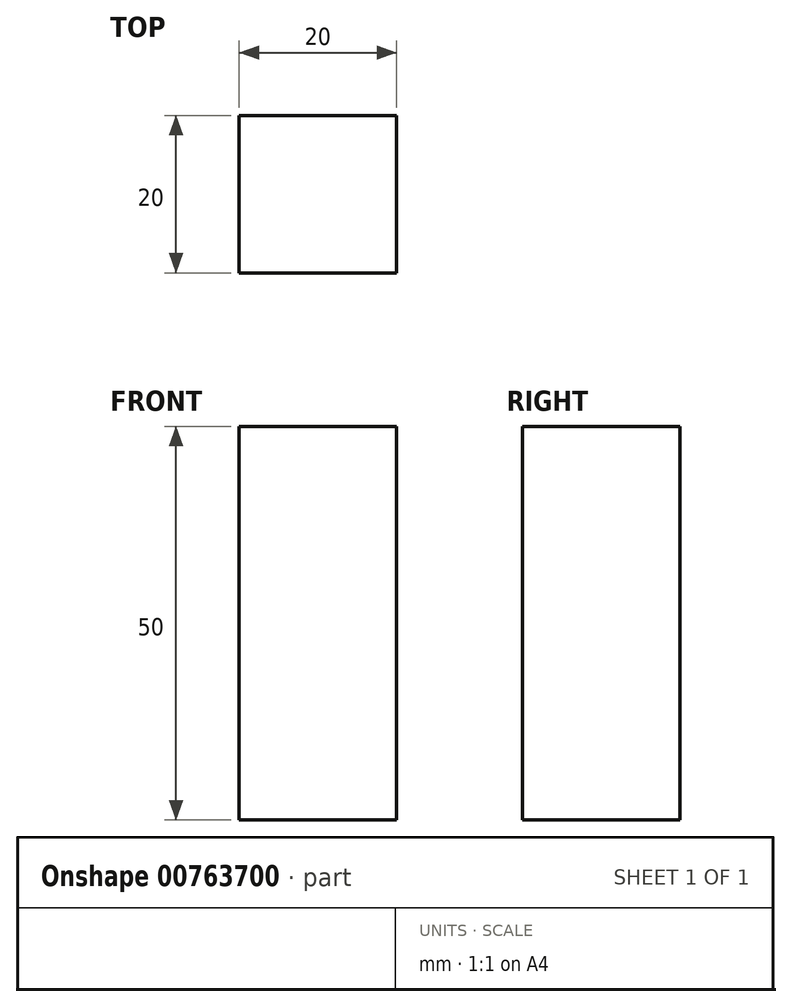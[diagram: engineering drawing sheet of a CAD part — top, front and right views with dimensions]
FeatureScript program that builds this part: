
annotation { "Feature Type Name" : "Feature", "Feature Type Description" : "" }
export const myFeature = defineFeature(function(context is Context, id is Id, definition is map)
    precondition{}
    {
        {
            var Q0;
            Q0=qCreatedBy(makeId("Top.planeOp"),FACE);
            var sketch = newSketch(context, id + "F0", { "sketchPlane" : qUnion([Q0])});
            skLineSegment(sketch, "E0.bottom", {"start": v(10, -10) * mm, "end": v(-10, -10) * mm});
            skLineSegment(sketch, "E0.top", {"start": v(10, 10) * mm, "end": v(-10, 10) * mm});
            skLineSegment(sketch, "E0.left", {"start": v(10, -10) * mm, "end": v(10, 10) * mm});
            skLineSegment(sketch, "E0.right", {"start": v(-10, -10) * mm, "end": v(-10, 10) * mm});
            skPoint(sketch, "E0.middle", {"position": v(0, 0) * mm});
            skSolve(sketch);
        }
        {
            var Q0;
            Q0 = qSketchRegion(id + "F0", true);
            extrude(context, id + "F1", {"entities" : qUnion([Q0]), "depth" : 50 * mm, "offsetDistance" : 25.4 * mm});
        }
    });
